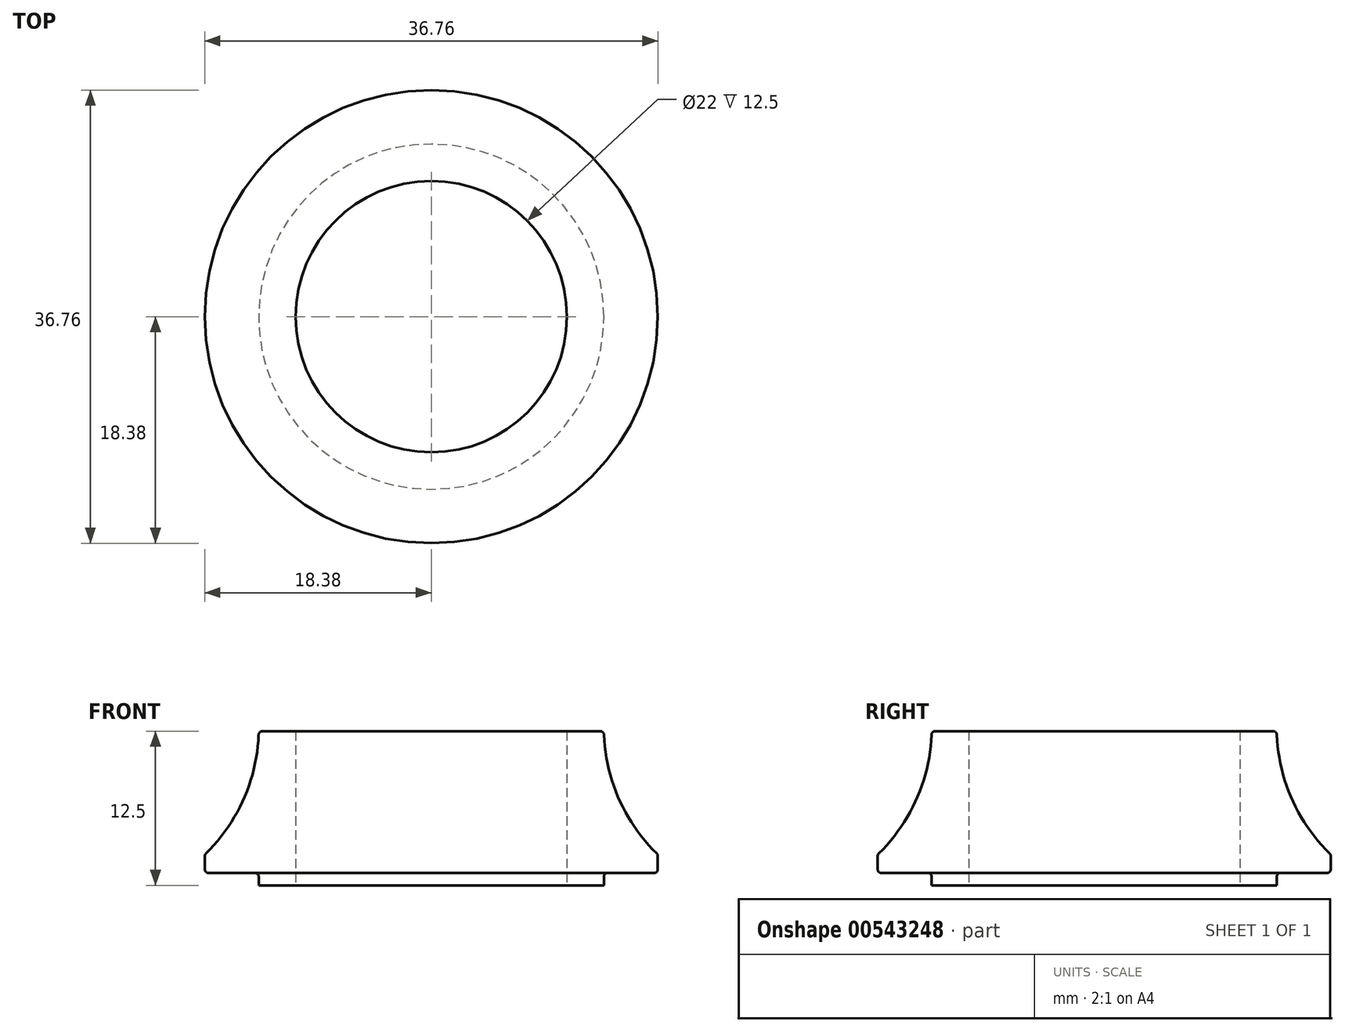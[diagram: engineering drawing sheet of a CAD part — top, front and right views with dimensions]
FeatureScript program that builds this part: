
annotation { "Feature Type Name" : "Feature", "Feature Type Description" : "" }
export const myFeature = defineFeature(function(context is Context, id is Id, definition is map)
    precondition{}
    {
        {
            var Q0;
            Q0=qCreatedBy(makeId("Front.planeOp"),FACE);
            var sketch = newSketch(context, id + "F0", { "sketchPlane" : qUnion([Q0])});
            skLineSegment(sketch, "E0", {"start": v(0, 0) * mm, "end": v(11, 0) * mm});
            skLineSegment(sketch, "E1", {"start": v(11, 0) * mm, "end": v(11, 12.5) * mm});
            skLineSegment(sketch, "E2", {"start": v(11, 12.5) * mm, "end": v(14, 12.5) * mm});
            skLineSegment(sketch, "E3", {"start": v(11, 0) * mm, "end": v(14, 0) * mm});
            skLineSegment(sketch, "E4", {"start": v(14, 0) * mm, "end": v(14, 1) * mm});
            skLineSegment(sketch, "E5", {"start": v(14, 1) * mm, "end": v(18.38, 1) * mm});
            skLineSegment(sketch, "E6", {"start": v(18.38, 1) * mm, "end": v(18.38, 2.5) * mm});
            skArc(sketch, "E7", {"start": v(14, 12.5) * mm, "mid": v(15.2, 7.07) * mm, "end": v(18.38, 2.5) * mm});
            skLineSegment(sketch, "E8", {"start": v(0, 0) * mm, "end": v(0, 15) * mm});
            skSolve(sketch);
        }
        {
            var Q0;
            Q0=makeQuery(id+"F0.imprint","IMPRINT",FACE,{"disambiguationData":[TD([[makeQuery(id+"F0.imprint","IMPRINT",EDGE,{"derivedFrom":sQuery(id+"F0.wireOp",EDGE,"E1")}),-1.0]])]});
            var Q1;
            Q1=sQuery(id+"F0.wireOp",EDGE,"E8");
            revolve(context, id + "F1", {"entities" : qUnion([Q0]), "axis" : qUnion([Q1]), "revolveType" : RevolveType.FULL});
        }
        {
            var Q0;
            Q0=makeQuery(id+"F1.opRevolve","SWEPT_EDGE",EDGE,{"disambiguationData":[OSD([sQuery(id+"F0.wireOp",EDGE,"E6"),sQuery(id+"F0.wireOp",EDGE,"E7")])]});
            var Q1;
            Q1=makeQuery(id+"F1.opRevolve","SWEPT_EDGE",EDGE,{"disambiguationData":[OSD([sQuery(id+"F0.wireOp",EDGE,"E5"),sQuery(id+"F0.wireOp",EDGE,"E6")])]});
            var Q2;
            Q2=makeQuery(id+"F1.opRevolve","SWEPT_EDGE",EDGE,{"disambiguationData":[OSD([sQuery(id+"F0.wireOp",EDGE,"E2"),sQuery(id+"F0.wireOp",EDGE,"E7")])]});
            var Q3;
            Q3=makeQuery(id+"F1.opRevolve","SWEPT_EDGE",EDGE,{"disambiguationData":[OSD([sQuery(id+"F0.wireOp",EDGE,"E4"),sQuery(id+"F0.wireOp",EDGE,"E5")])]});
            fillet(context, id + "F2", {"entities" : qUnion([Q0, Q1, Q2, Q3]), "radius" : 0.3 * mm, "tangentPropagation" : true, "allowEdgeOverflow" : false});
        }
    });
